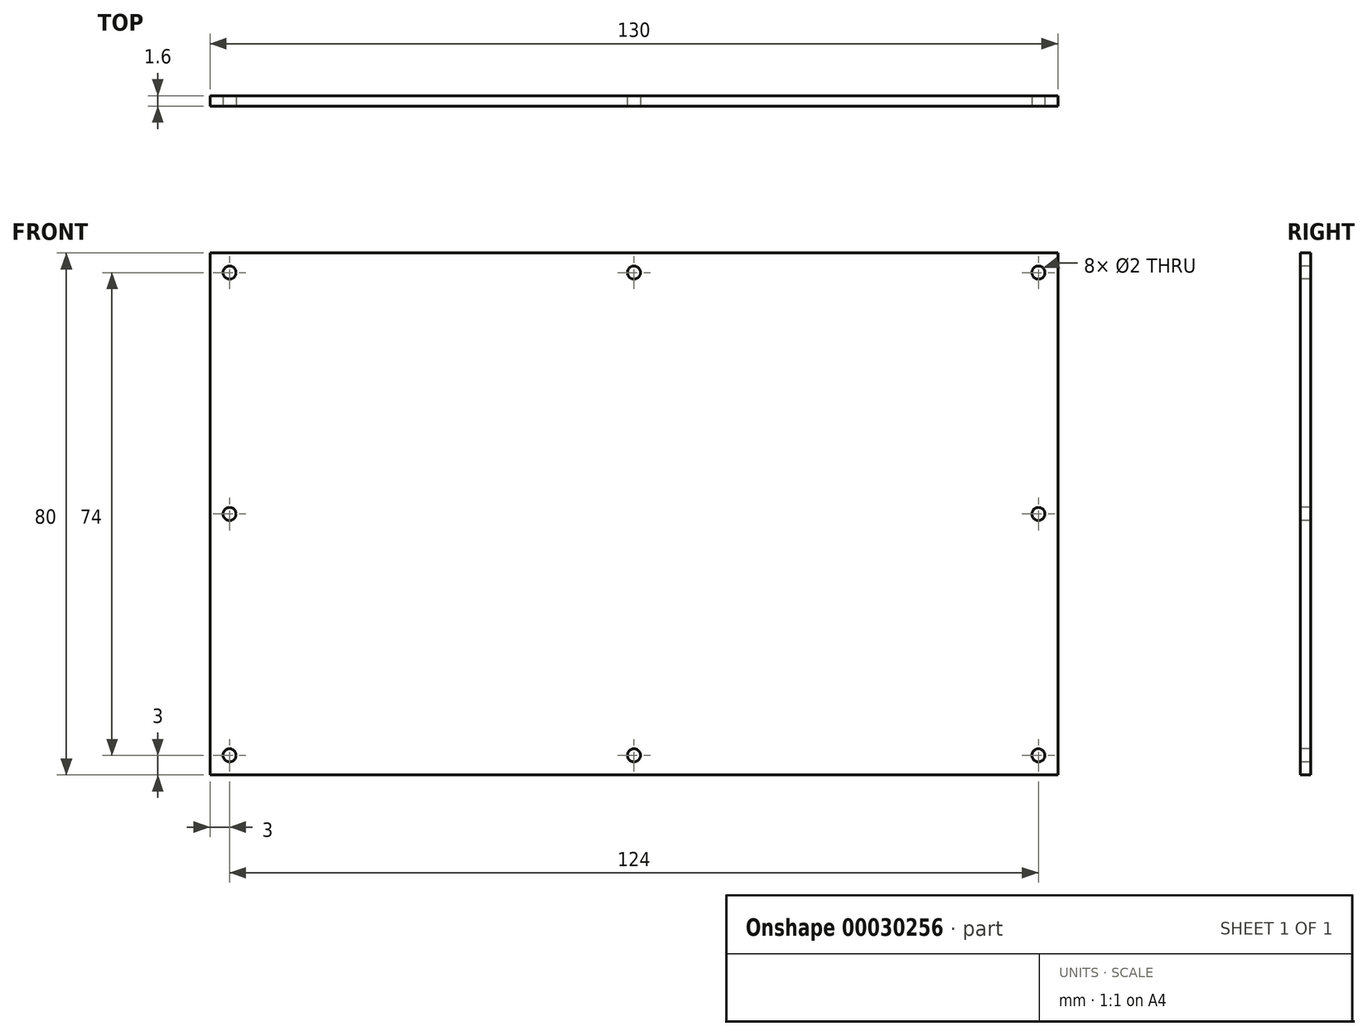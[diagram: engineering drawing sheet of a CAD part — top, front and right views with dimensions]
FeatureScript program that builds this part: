
annotation { "Feature Type Name" : "Feature", "Feature Type Description" : "" }
export const myFeature = defineFeature(function(context is Context, id is Id, definition is map)
    precondition{}
    {
        {
            var Q0;
            Q0=qCreatedBy(makeId("Front.planeOp"),FACE);
            var sketch = newSketch(context, id + "F0", { "sketchPlane" : qUnion([Q0])});
            skLineSegment(sketch, "E0.bottom", {"start": v(65, 40) * mm, "end": v(-65, 40) * mm});
            skLineSegment(sketch, "E0.top", {"start": v(65, -40) * mm, "end": v(-65, -40) * mm});
            skLineSegment(sketch, "E0.left", {"start": v(65, 40) * mm, "end": v(65, -40) * mm});
            skLineSegment(sketch, "E0.right", {"start": v(-65, 40) * mm, "end": v(-65, -40) * mm});
            skPoint(sketch, "E1", {"position": v(62, 37) * mm});
            skPoint(sketch, "E2.MirrorP", {"position": v(62, -37) * mm});
            skPoint(sketch, "E3.MirrorP", {"position": v(-62, 37) * mm});
            skPoint(sketch, "E4.MirrorP", {"position": v(-62, -37) * mm});
            skPoint(sketch, "E5", {"position": v(-62, 0) * mm});
            skPoint(sketch, "E6.MirrorP", {"position": v(62, 0) * mm});
            skPoint(sketch, "E7", {"position": v(0, -37) * mm});
            skPoint(sketch, "E8.MirrorP", {"position": v(0, 37) * mm});
            skSolve(sketch);
        }
        {
            var Q0;
            Q0=makeQuery(id+"F0.imprint","IMPRINT",FACE,{"disambiguationData":[TD([[makeQuery(id+"F0.imprint","IMPRINT",EDGE,{"derivedFrom":sQuery(id+"F0.wireOp",EDGE,"E0.bottom")}),1.0]])]});
            extrude(context, id + "F1", {"entities" : qUnion([Q0]), "oppositeDirection" : true, "depth" : 1.6 * mm});
        }
        {
            var Q0;
            Q0=sQuery(id+"F0.wireOp",VERTEX,"E3.MirrorP");
            var Q1;
            Q1=sQuery(id+"F0.wireOp",VERTEX,"E8.MirrorP");
            var Q2;
            Q2=sQuery(id+"F0.wireOp",VERTEX,"E1");
            var Q3;
            Q3=sQuery(id+"F0.wireOp",VERTEX,"E6.MirrorP");
            var Q4;
            Q4=sQuery(id+"F0.wireOp",VERTEX,"E2.MirrorP");
            var Q5;
            Q5=sQuery(id+"F0.wireOp",VERTEX,"E7");
            var Q6;
            Q6=sQuery(id+"F0.wireOp",VERTEX,"E4.MirrorP");
            var Q7;
            Q7=sQuery(id+"F0.wireOp",VERTEX,"E5");
            var Q8;
            Q8=makeQuery(id+"F1.opExtrude","SWEPT_BODY",BODY,{"disambiguationData":[OSD([sQuery(id+"F0.wireOp",EDGE,"E0.bottom"),sQuery(id+"F0.wireOp",EDGE,"E0.top"),sQuery(id+"F0.wireOp",EDGE,"E0.left"),sQuery(id+"F0.wireOp",EDGE,"E0.right")])]});
            hole(context, id + "F2", {"style" : HoleStyle.SIMPLE, "endStyle" : HoleEndStyle.THROUGH, "holeDiameter" : 2 * mm, "tappedDepth" : 12 * mm, "tapClearance" : 3, "locations" : qUnion([Q0, Q1, Q2, Q3, Q4, Q5, Q6, Q7]), "scope" : qUnion([Q8])});
        }
    });
